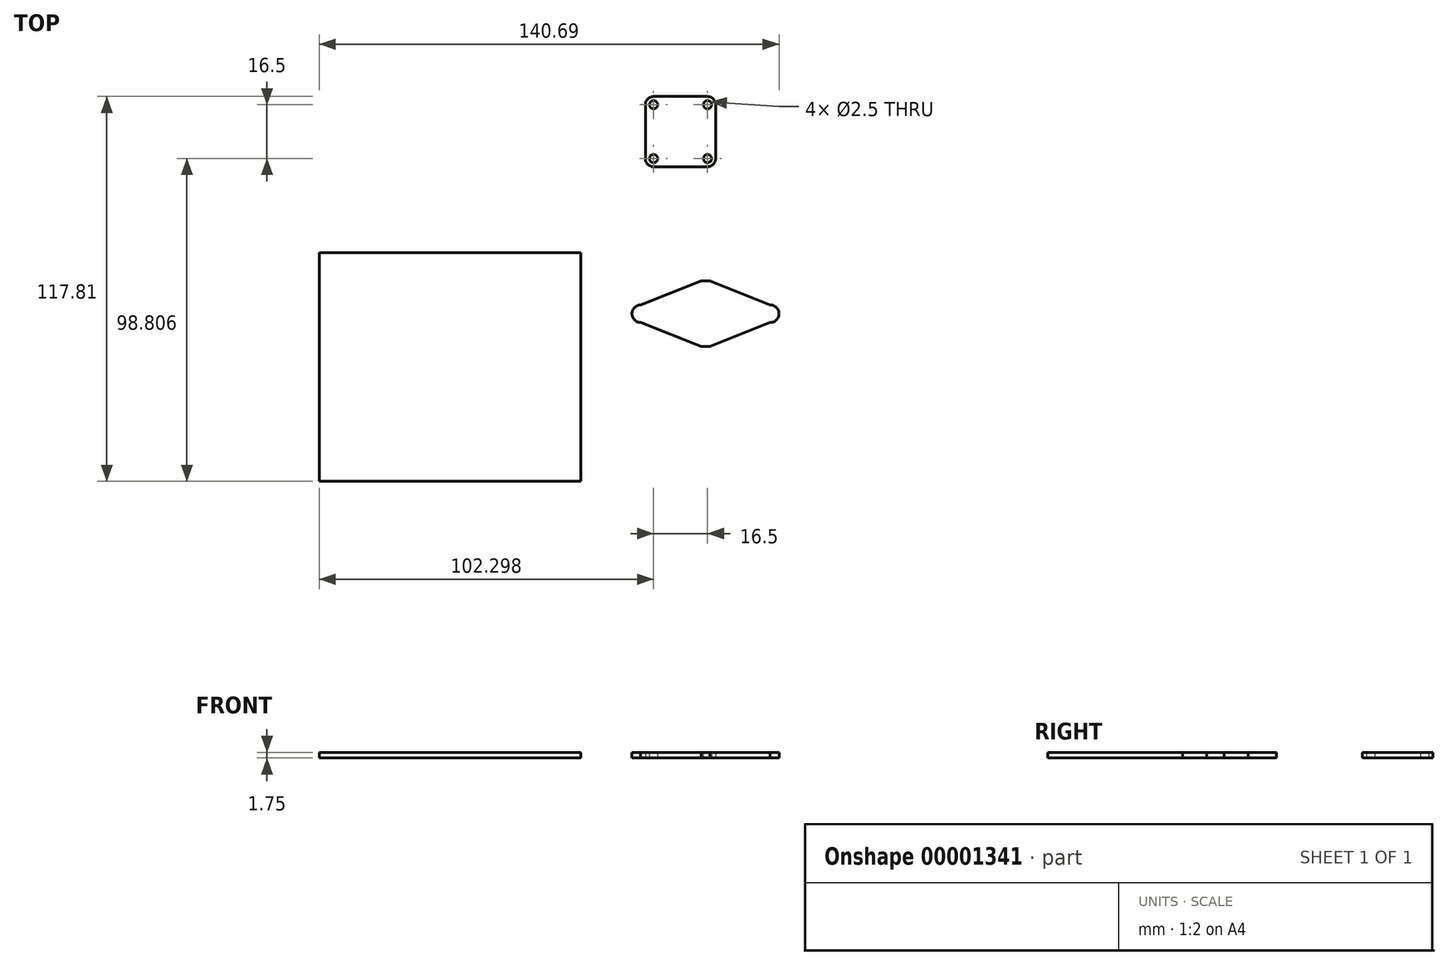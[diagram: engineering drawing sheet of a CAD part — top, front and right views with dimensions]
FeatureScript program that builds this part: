
annotation { "Feature Type Name" : "Feature", "Feature Type Description" : "" }
export const myFeature = defineFeature(function(context is Context, id is Id, definition is map)
    precondition{}
    {
        {
            var Q0;
            Q0=qCreatedBy(makeId("Top.planeOp"),FACE);
            var sketch = newSketch(context, id + "F0", { "sketchPlane" : qUnion([Q0])});
            skLineSegment(sketch, "E0.bottom", {"start": v(-80, -70) * mm, "end": v(0, -70) * mm});
            skLineSegment(sketch, "E0.top", {"start": v(-80, 0) * mm, "end": v(0, 0) * mm});
            skLineSegment(sketch, "E0.left", {"start": v(-80, -70) * mm, "end": v(-80, 0) * mm});
            skLineSegment(sketch, "E0.right", {"start": v(0, -70) * mm, "end": v(0, 0) * mm});
            skSolve(sketch);
        }
        {
            var Q0;
            Q0=makeQuery(id+"F0.imprint","IMPRINT",FACE,{"disambiguationData":[TD([[makeQuery(id+"F0.imprint","IMPRINT",EDGE,{"derivedFrom":sQuery(id+"F0.wireOp",EDGE,"E0.bottom")}),1.0]])]});
            extrude(context, id + "F1", {"entities" : qUnion([Q0]), "depth" : 1.75 * mm});
        }
        {
            var Q0;
            Q0=qCreatedBy(makeId("Top.planeOp"),FACE);
            var sketch = newSketch(context, id + "F2", { "sketchPlane" : qUnion([Q0])});
            skLineSegment(sketch, "E1.bottom", {"start": v(38.8, 47.8) * mm, "end": v(22.3, 47.8) * mm});
            skLineSegment(sketch, "E1.top", {"start": v(38.8, 26.3) * mm, "end": v(22.3, 26.3) * mm});
            skLineSegment(sketch, "E1.left", {"start": v(41.3, 45.3) * mm, "end": v(41.3, 28.8) * mm});
            skLineSegment(sketch, "E1.right", {"start": v(19.8, 45.3) * mm, "end": v(19.8, 28.8) * mm});
            skPoint(sketch, "E2.visualSharp", {"position": v(19.8, 47.8) * mm});
            skArc(sketch, "E2.filletArc", {"start": v(22.3, 47.8) * mm, "mid": v(20.53, 47.07) * mm, "end": v(19.8, 45.3) * mm});
            skPoint(sketch, "E3.visualSharp", {"position": v(19.8, 26.3) * mm});
            skArc(sketch, "E3.filletArc", {"start": v(19.8, 28.8) * mm, "mid": v(20.53, 27.04) * mm, "end": v(22.3, 26.3) * mm});
            skPoint(sketch, "E4.visualSharp", {"position": v(41.3, 26.3) * mm});
            skArc(sketch, "E4.filletArc", {"start": v(38.8, 26.3) * mm, "mid": v(40.57, 27.04) * mm, "end": v(41.3, 28.8) * mm});
            skPoint(sketch, "E5.visualSharp", {"position": v(41.3, 47.8) * mm});
            skArc(sketch, "E5.filletArc", {"start": v(41.3, 45.3) * mm, "mid": v(40.57, 47.07) * mm, "end": v(38.8, 47.8) * mm});
            skCircle(sketch, "E6", {"center": v(22.3, 28.8) * mm, "radius": 1.25 * mm});
            skCircle(sketch, "E7", {"center": v(38.8, 28.8) * mm, "radius": 1.25 * mm});
            skCircle(sketch, "E8", {"center": v(38.8, 45.3) * mm, "radius": 1.25 * mm});
            skCircle(sketch, "E9", {"center": v(22.3, 45.3) * mm, "radius": 1.25 * mm});
            skSolve(sketch);
        }
        {
            var Q0;
            Q0=makeQuery(id+"F2.imprint","IMPRINT",FACE,{"disambiguationData":[TD([[makeQuery(id+"F2.imprint","IMPRINT",EDGE,{"derivedFrom":sQuery(id+"F2.wireOp",EDGE,"E1.bottom")}),1.0]])]});
            extrude(context, id + "F3", {"entities" : qUnion([Q0]), "depth" : 1.75 * mm});
        }
        {
            var Q0;
            Q0=qCreatedBy(makeId("Top.planeOp"),FACE);
            var sketch = newSketch(context, id + "F4", { "sketchPlane" : qUnion([Q0])});
            skArc(sketch, "E10", {"start": v(18.38, -16) * mm, "mid": v(15.7, -18.7) * mm, "end": v(18.38, -21.38) * mm});
            skArc(sketch, "E11", {"start": v(58, -21.38) * mm, "mid": v(60.7, -18.7) * mm, "end": v(58, -16) * mm});
            skLineSegment(sketch, "E12", {"start": v(18.38, -16) * mm, "end": v(36.85, -8.7) * mm});
            skLineSegment(sketch, "E13", {"start": v(36.85, -8.7) * mm, "end": v(39.54, -8.7) * mm});
            skLineSegment(sketch, "E14", {"start": v(39.54, -8.7) * mm, "end": v(58, -16) * mm});
            skLineSegment(sketch, "E15", {"start": v(18.38, -21.38) * mm, "end": v(36.85, -28.7) * mm});
            skLineSegment(sketch, "E16", {"start": v(36.85, -28.7) * mm, "end": v(39.54, -28.7) * mm});
            skLineSegment(sketch, "E17", {"start": v(39.54, -28.7) * mm, "end": v(58, -21.38) * mm});
            skLineSegment(sketch, "E18", {"start": v(18.38, -18.7) * mm, "end": v(58, -18.7) * mm, "construction": true});
            skLineSegment(sketch, "E19", {"start": v(36.85, -8.7) * mm, "end": v(36.85, -18.7) * mm, "construction": true});
            skLineSegment(sketch, "E20", {"start": v(36.85, -18.7) * mm, "end": v(36.85, -28.7) * mm, "construction": true});
            skSolve(sketch);
        }
        {
            var Q0;
            Q0=makeQuery(id+"F4.imprint","IMPRINT",FACE,{"disambiguationData":[TD([[makeQuery(id+"F4.imprint","IMPRINT",EDGE,{"derivedFrom":sQuery(id+"F4.wireOp",EDGE,"173541d4-966b-4354-8360-a031c9ccc219.bottom")}),1.0]])]});
            var Q1;
            Q1=makeQuery(id+"F4.imprint","IMPRINT",FACE,{"disambiguationData":[TD([[makeQuery(id+"F4.imprint","IMPRINT",EDGE,{"derivedFrom":sQuery(id+"F4.wireOp",EDGE,"E10")}),1.0]])]});
            extrude(context, id + "F5", {"entities" : qUnion([Q0, Q1]), "depth" : 1.75 * mm});
        }
    });
